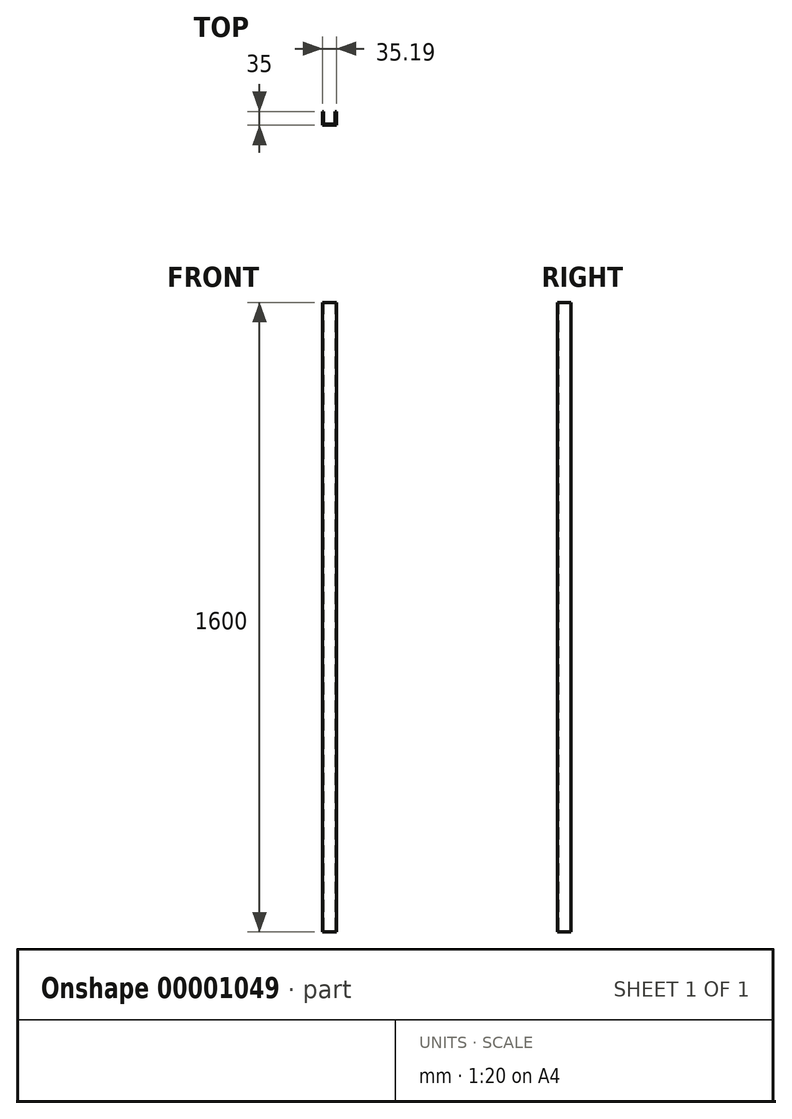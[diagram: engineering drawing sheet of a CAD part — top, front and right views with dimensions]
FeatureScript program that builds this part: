
annotation { "Feature Type Name" : "Feature", "Feature Type Description" : "" }
export const myFeature = defineFeature(function(context is Context, id is Id, definition is map)
    precondition{}
    {
        {
            var Q0;
            Q0=qCreatedBy(makeId("Top.planeOp"),FACE);
            var sketch = newSketch(context, id + "F0", { "sketchPlane" : qUnion([Q0])});
            skLineSegment(sketch, "E0", {"start": v(-58.49, -35) * mm, "end": v(-23.49, -35) * mm});
            skLineSegment(sketch, "E1", {"start": v(-23.49, -35) * mm, "end": v(-23.49, 0) * mm});
            skLineSegment(sketch, "E2", {"start": v(-23.49, 0) * mm, "end": v(-26.49, 0) * mm});
            skLineSegment(sketch, "E3", {"start": v(-26.49, 0) * mm, "end": v(-26.49, -29) * mm});
            skLineSegment(sketch, "E4", {"start": v(-29.49, -32) * mm, "end": v(-52.68, -32) * mm});
            skLineSegment(sketch, "E5", {"start": v(-55.68, -29) * mm, "end": v(-55.68, 0) * mm});
            skLineSegment(sketch, "E6", {"start": v(-55.68, 0) * mm, "end": v(-58.68, 0) * mm});
            skLineSegment(sketch, "E7", {"start": v(-58.68, 0) * mm, "end": v(-58.49, -35) * mm});
            skPoint(sketch, "E8.visualSharp", {"position": v(-55.68, -32) * mm});
            skArc(sketch, "E8.filletArc", {"start": v(-55.68, -29) * mm, "mid": v(-54.8, -31.12) * mm, "end": v(-52.68, -32) * mm});
            skPoint(sketch, "E9.visualSharp", {"position": v(-26.49, -32) * mm});
            skArc(sketch, "E9.filletArc", {"start": v(-29.49, -32) * mm, "mid": v(-27.36, -31.12) * mm, "end": v(-26.49, -29) * mm});
            skSolve(sketch);
        }
        {
            var Q0;
            Q0=makeQuery(id+"F0.imprint","IMPRINT",FACE,{"disambiguationData":[TD([[makeQuery(id+"F0.imprint","IMPRINT",EDGE,{"derivedFrom":sQuery(id+"F0.wireOp",EDGE,"E0")}),1.0]])]});
            extrude(context, id + "F1", {"entities" : qUnion([Q0]), "depth" : 1600 * mm});
        }
    });
